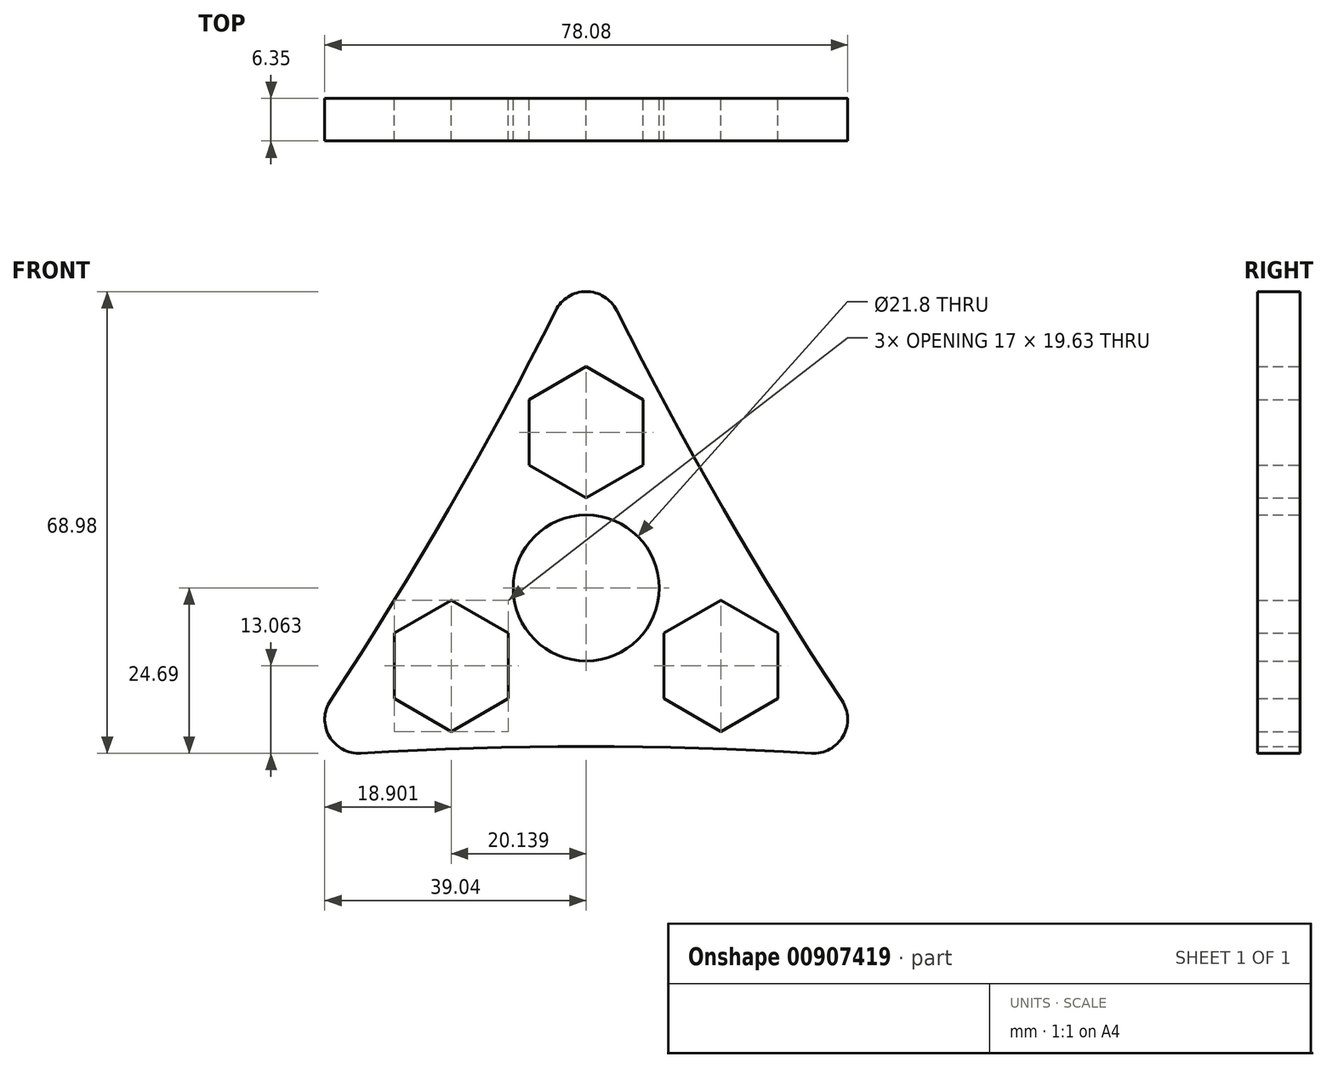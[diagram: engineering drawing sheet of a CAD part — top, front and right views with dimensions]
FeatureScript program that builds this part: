
annotation { "Feature Type Name" : "Feature", "Feature Type Description" : "" }
export const myFeature = defineFeature(function(context is Context, id is Id, definition is map)
    precondition{}
    {
        {
            var Q0;
            Q0=qCreatedBy(makeId("Front.planeOp"),FACE);
            var sketch = newSketch(context, id + "F0", { "sketchPlane" : qUnion([Q0])});
            skArc(sketch, "E0", {"start": v(-44, -25.4) * mm, "mid": v(-20.5, 11.83) * mm, "end": v(0, 50.8) * mm});
            skArc(sketch, "E1.MirrorCS", {"start": v(44, -25.4) * mm, "mid": v(20.5, 11.83) * mm, "end": v(0, 50.8) * mm});
            skArc(sketch, "E2.MirrorCS", {"start": v(44, -25.4) * mm, "mid": v(0, -23.66) * mm, "end": v(-44, -25.4) * mm});
            skCircle(sketch, "E3.cCircle", {"center": v(0, 23.25) * mm, "radius": 8.5 * mm, "construction": true});
            skLineSegment(sketch, "E3.0", {"start": v(-8.5, 18.35) * mm, "end": v(-8.5, 28.16) * mm});
            skLineSegment(sketch, "E3.1", {"start": v(-8.5, 28.16) * mm, "end": v(0, 33.07) * mm});
            skLineSegment(sketch, "E3.2", {"start": v(0, 33.07) * mm, "end": v(8.5, 28.16) * mm});
            skLineSegment(sketch, "E3.3", {"start": v(8.5, 28.16) * mm, "end": v(8.5, 18.35) * mm});
            skLineSegment(sketch, "E3.4", {"start": v(8.5, 18.35) * mm, "end": v(0, 13.44) * mm});
            skLineSegment(sketch, "E3.5", {"start": v(0, 13.44) * mm, "end": v(-8.5, 18.35) * mm});
            skPoint(sketch, "E3.0.midPoint", {"position": v(-8.5, 23.25) * mm});
            skLineSegment(sketch, "E4.1.0", {"start": v(-20.14, -21.44) * mm, "end": v(-28.64, -16.53) * mm});
            skLineSegment(sketch, "E4.1.1", {"start": v(-11.64, -16.53) * mm, "end": v(-20.14, -21.44) * mm});
            skLineSegment(sketch, "E4.1.2", {"start": v(-11.64, -6.72) * mm, "end": v(-11.64, -16.53) * mm});
            skLineSegment(sketch, "E4.1.3", {"start": v(-20.14, -1.81) * mm, "end": v(-11.64, -6.72) * mm});
            skLineSegment(sketch, "E4.1.4", {"start": v(-28.64, -6.72) * mm, "end": v(-20.14, -1.81) * mm});
            skLineSegment(sketch, "E4.1.5", {"start": v(-28.64, -16.53) * mm, "end": v(-28.64, -6.72) * mm});
            skLineSegment(sketch, "E4.2.0", {"start": v(28.64, -6.72) * mm, "end": v(28.64, -16.53) * mm});
            skLineSegment(sketch, "E4.2.1", {"start": v(20.14, -1.81) * mm, "end": v(28.64, -6.72) * mm});
            skLineSegment(sketch, "E4.2.2", {"start": v(11.64, -6.72) * mm, "end": v(20.14, -1.81) * mm});
            skLineSegment(sketch, "E4.2.3", {"start": v(11.64, -16.53) * mm, "end": v(11.64, -6.72) * mm});
            skLineSegment(sketch, "E4.2.4", {"start": v(20.14, -21.44) * mm, "end": v(11.64, -16.53) * mm});
            skLineSegment(sketch, "E4.2.5", {"start": v(28.64, -16.53) * mm, "end": v(20.14, -21.44) * mm});
            skPoint(sketch, "E4.center", {"position": v(0, 0) * mm});
            skCircle(sketch, "E5", {"center": v(0, 0) * mm, "radius": 10.9 * mm});
            skSolve(sketch);
        }
        {
            var Q0;
            Q0 = qSketchRegion(id + "F0", true);
            extrude(context, id + "F1", {"entities" : qUnion([Q0]), "depth" : 6.35 * mm, "offsetDistance" : 25.4 * mm});
        }
        {
            var Q0;
            Q0=makeQuery(id+"F1.opExtrude","SWEPT_EDGE",EDGE,{"disambiguationData":[OSD([sQuery(id+"F0.wireOp",EDGE,"DTGijesI-Etz5-2gqr-Ztja-8alHDgAm9SFy"),sQuery(id+"F0.wireOp",EDGE,"E0"),sQuery(id+"F0.wireOp",EDGE,"E2.MirrorCS")])]});
            var Q1;
            Q1=makeQuery(id+"F1.opExtrude","SWEPT_EDGE",EDGE,{"disambiguationData":[OSD([sQuery(id+"F0.wireOp",EDGE,"zcRCdeGX-igEz-lsSw-sWEx-I6tDbqrJ4Ukh"),sQuery(id+"F0.wireOp",EDGE,"E1.MirrorCS"),sQuery(id+"F0.wireOp",EDGE,"E2.MirrorCS")])]});
            var Q2;
            Q2=makeQuery(id+"F1.opExtrude","SWEPT_EDGE",EDGE,{"disambiguationData":[OSD([sQuery(id+"F0.wireOp",EDGE,"fXWrS5rX-QChu-gcRg-vKrF-DexGNgl1Ey69"),sQuery(id+"F0.wireOp",EDGE,"E0"),sQuery(id+"F0.wireOp",EDGE,"E1.MirrorCS")])]});
            fillet(context, id + "F2", {"entities" : qUnion([Q0, Q1, Q2]), "radius" : 5.08 * mm, "tangentPropagation" : true, "allowEdgeOverflow" : false});
        }
    });
